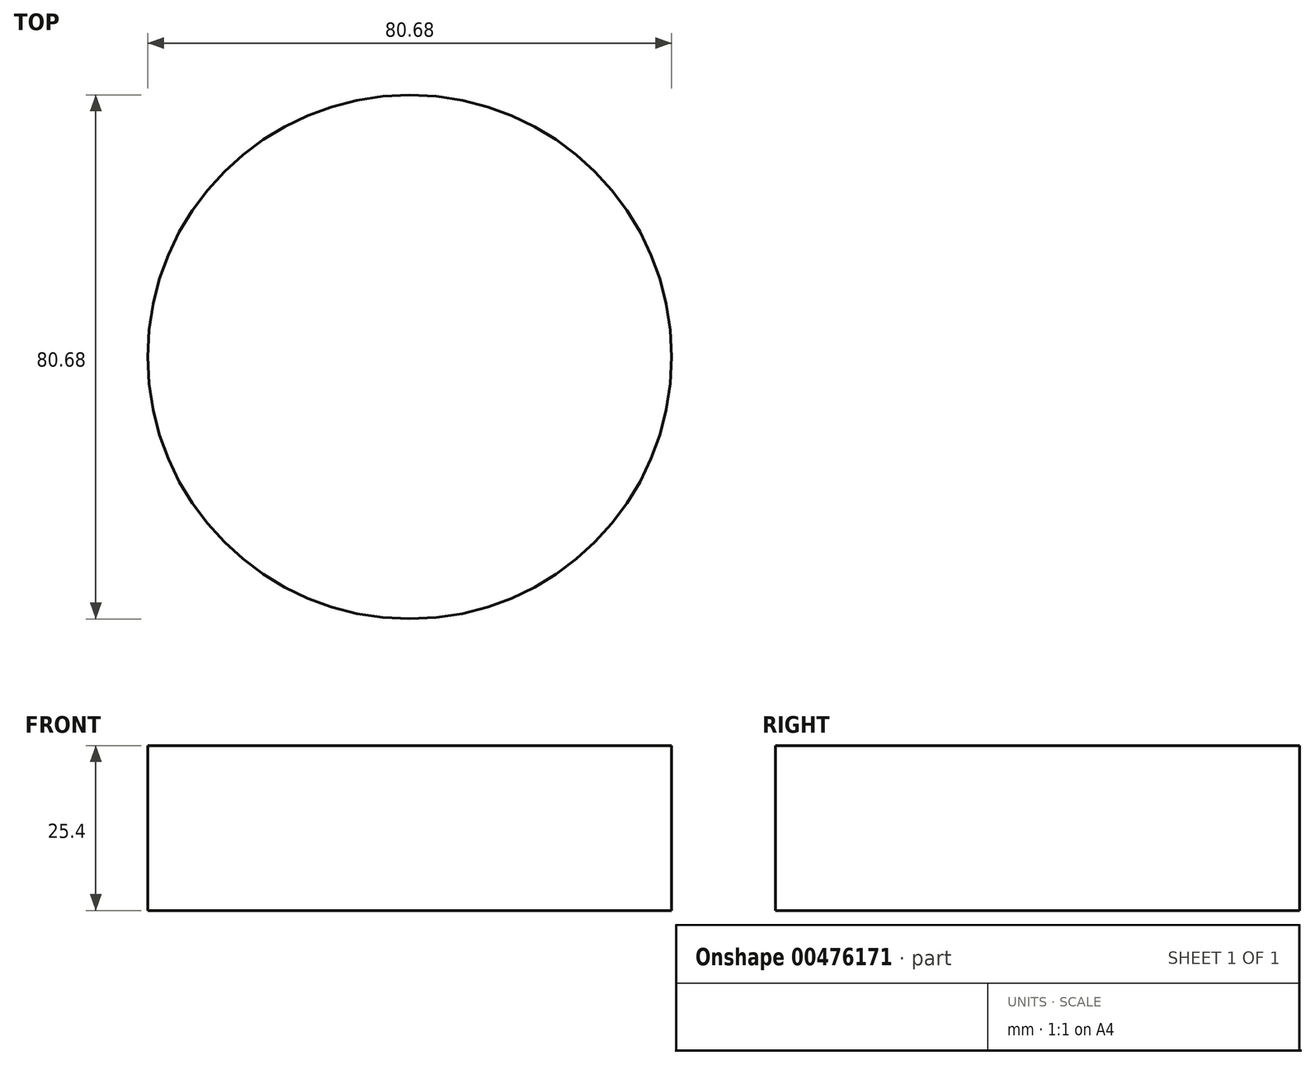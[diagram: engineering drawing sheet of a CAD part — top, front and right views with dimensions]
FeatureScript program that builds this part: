
annotation { "Feature Type Name" : "Feature", "Feature Type Description" : "" }
export const myFeature = defineFeature(function(context is Context, id is Id, definition is map)
    precondition{}
    {
        {
            var Q0;
            Q0=qCreatedBy(makeId("Top.planeOp"),FACE);
            var sketch = newSketch(context, id + "F0", { "sketchPlane" : qUnion([Q0])});
            skCircle(sketch, "E0", {"center": v(0, 0) * mm, "radius": 40.34 * mm});
            skSolve(sketch);
        }
        {
            var Q0;
            Q0 = qSketchRegion(id + "F0", true);
            extrude(context, id + "F1", {"entities" : qUnion([Q0]), "depth" : 25.4 * mm});
        }
    });
